# Revit family: v-142_143bzlt5_60Hz
name_source: partatom
category: 機械設備
units: mm (PartAtom-declared; Revit-internal decimal feet)

## family parameters
OmniClass タイトル = Centrifugal Fans
OmniClass 番号 = 23.75.35.17.27
パーツ タイプ = 標準
ロード時にボイドで切り取り = いいえ
丸型コネクタ寸法 = 直径を使用
作業面ベース = いいえ
共有 = いいえ
常に垂直 = はい
部屋計算ポイント = はい

## types (2) — shared parameters
D1 = 472
Depth = 400  [stored 1.31234 ft]
DuctChange_D = 54
Duct_Depth = 61  [stored 0.200131 ft]
Duct_H = 107  [stored 0.35105 ft]
Duct_RA_EA_W = 70  [stored 0.229659 ft]
EAサイズ_D = 98
H1 = 39  [stored 0.127953 ft]
Height = 170  [stored 0.557743 ft]
IfcExportAs = IfcFanType
IfcExportType = PROPELLORAXIAL
MAX静圧 = 0.0 Pa
MAX風量 = 170.0 m³/h
MID静圧 = 0.0 Pa
MID風量 = 0.0 m³/h
MIN静圧 = 0.0 Pa
MIN風量 = 90.0 m³/h
OmniClassCode = 23-33 31 19 11 15
RAサイズ_D = 98
RAダクト接続口_A = はい
RAダクト接続口_C = いいえ
URL = https://www.mitsubishielectric.co.jp
Uniclass2015Code = Pr_65_67_29_12
Uniclass2015Title = Centrifugal fans
Uniclass2015Version = Systems v1.9
W1 = 372  [stored 1.22047 ft]
Width = 280  [stored 0.918635 ft]
カバーマテリアル = 合成樹脂(白)
ダクト径 = 100 mm
マテリアル = 亜鉛メッキ鋼板
仕様書バージョン = Version1.0
企業コード = 108420
分類コード = 50052503100080
周波数 = 60 Hz
呼称 = 天井扇
本体固定用穴ピッチ1 = 304  [stored 0.997375 ft]
本体固定用穴ピッチ2 = 265  [stored 0.869423 ft]
本体固定用穴ピッチ3 = 224  [stored 0.734908 ft]
本体固定用穴ピッチ4 = 424  [stored 1.39108 ft]
極数 = 2
法定耐用年数 = 10
消費電力 = 1230 W
点検口 = はい
点検口_Depth = 450  [stored 1.47638 ft]
点検口離隔 = 150
相 = 1
積算_科目 = 2 換気設備
製品リリース年月 = 2022年5月10日
製品出荷対象 = 国内
製品質量 = 8.40 kg
製造元 = 三菱電機株式会社
設置方法 = カセット形
説明 = バス乾燥・暖房・換気システム 薄形タイプ
負荷分類 = 3_ファン類
質量 = 10.08 kg
運転質量 = 0.00 kg
電動機出力 = 0 W
電圧 = 100 V

## per-type parameters (varying)
| type | RAダクト接続口_B | 価格 |
| V-142BZLT5 | いいえ | 124300 $ |
| V-143BZLT5 | はい | 126500 $ |

note: column(s) folded — value = type name in every type: モデル

note: [stored X ft] marks values corroborated as IEEE doubles in the binary element streams (Revit-internal decimal feet)
